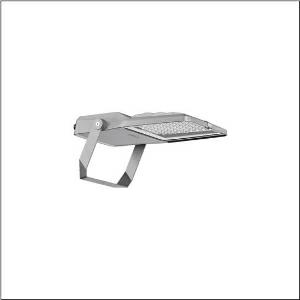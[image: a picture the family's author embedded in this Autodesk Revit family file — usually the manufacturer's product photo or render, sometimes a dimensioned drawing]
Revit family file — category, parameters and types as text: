
# Revit family: floodlight_fl_21_iq_mini___pl43_5xa7771d4a1a_5f3b
name_source: partatom
category: Lighting Fixtures
units: mm (PartAtom-declared; Revit-internal decimal feet)

## family parameters
Cut with Voids When Loaded = No
Host = Face
Light Source = No
Part Type = Normal
Room Calculation Point = No
Round Connector Dimension = Use Diameter
Shared = No

## types (1)
- --- (1 x LED, 19090 lm, 143 W, 4000K)
    Apparent Load = 143 VA
    CIE Flux Codes = 27 78 99 100 100
    Color Rendering = 70
    Color Temperature = 4000K
    Default Elevation = 1800 mm
    Description = Floodlight FL 21 iQ mini, floodlight, primary light control with lens, of PMMA, primary optical cover: protective disc, of toughened safety glass, transparent, light distribution: PL43, light emission: direct distribution, installation type: surface-mounted, LED, High Power LED, rated luminous flux: 19.090lm, luminous efficacy: 134lm/W, light colour: 740, colour temperature: 4000K, control gear: iQ Comfort/DALI, control: Auto-Match, Temp-Guard, Lumen-Switch, Night-Set, Smart-Wire, Light-Fading, Desk-Remote (wireless, voltage-free reading and setting of iQ features in the workshop via application-optimized NFC function/RFID function), optimised constant luminous flux control (CLO 2.0), with terminal, 6-pole, mains connection: 220..240V, AC, 50/60Hz, start of lifetime: 143W, end of service life: 152W, reduction: 61W, luminaire housing, of diecast aluminium, powder-coated, Siteco® metallic grey (DB 702S), corrosivity category C5 mid according to DIN EN ISO 12944, suitable for swimming pools, chlorine-resistant, sealing non-destructively replaceable, mounting bracket, of steel, galvanised, powder-coated, Siteco® metallic grey (DB 702S), protection rating (complete): IP66, insulation class (complete): insulation class II (safety insulation), certification: CE, ENEC, VDE, protection symbol: D, impact resistance: IK08, permissible operating ambient temperature: -40..+40°C, permissible operating ambient temperature for outdoor applications: -40..+50°C, standard: DIN EN 12944, LABS conformity tested according to VDMA 24364:2018-05, packaging unit: 1 piece

Light Distribution: PL43
    Height = 70 mm
    Lamp = 1 x LED
    Lamp Light Flux = 19090 lm
    Lamp Power = 143 W
    Lamp count = 1
    Length = 485 mm
    Luminous efficacy = 133 lm/W
    Manufacturer = Siteco
    ModVariant = No
    Model = 5XA7771D4A1A
    Number of Poles = 1
    OnlyDefault = Yes
    Power Factor = 1
    Product Name = Floodlight FL 21 iQ mini | PL43
    Product group = floodlight | pylon annexe
    ProductGroupID = 6200
    Protection Class = Protection class II
    Protection Degree = IP 66
    RLX_Detail_Level = 1
    RLX_Emergency_Light_Flux = 0 lm
    RLX_Emergency_Type = 0
    RLX_Emergency_Type_DB = No
    RlxData = <blob elided: 96597 chars, md5=fd8466af>
    Socket = socket
    Standby Power = 0 W
    System Light Flux = 19090 lm
    System Power = 143 W
    Type Comments = factory setting: luminous flux: 100 % | dim-lin: 254 | 730 mA
    Type Image = l_1006845.jpg
    URL = http://relux.com
    VarID = @adj_161398
    Voltage = 0 V
    Weight = 0.00 kg
    Width = 337 mm

## geometry (parser evidence)
native form markers: Blend x4, Sweep x11
no freeform markers — native parametric forms only
